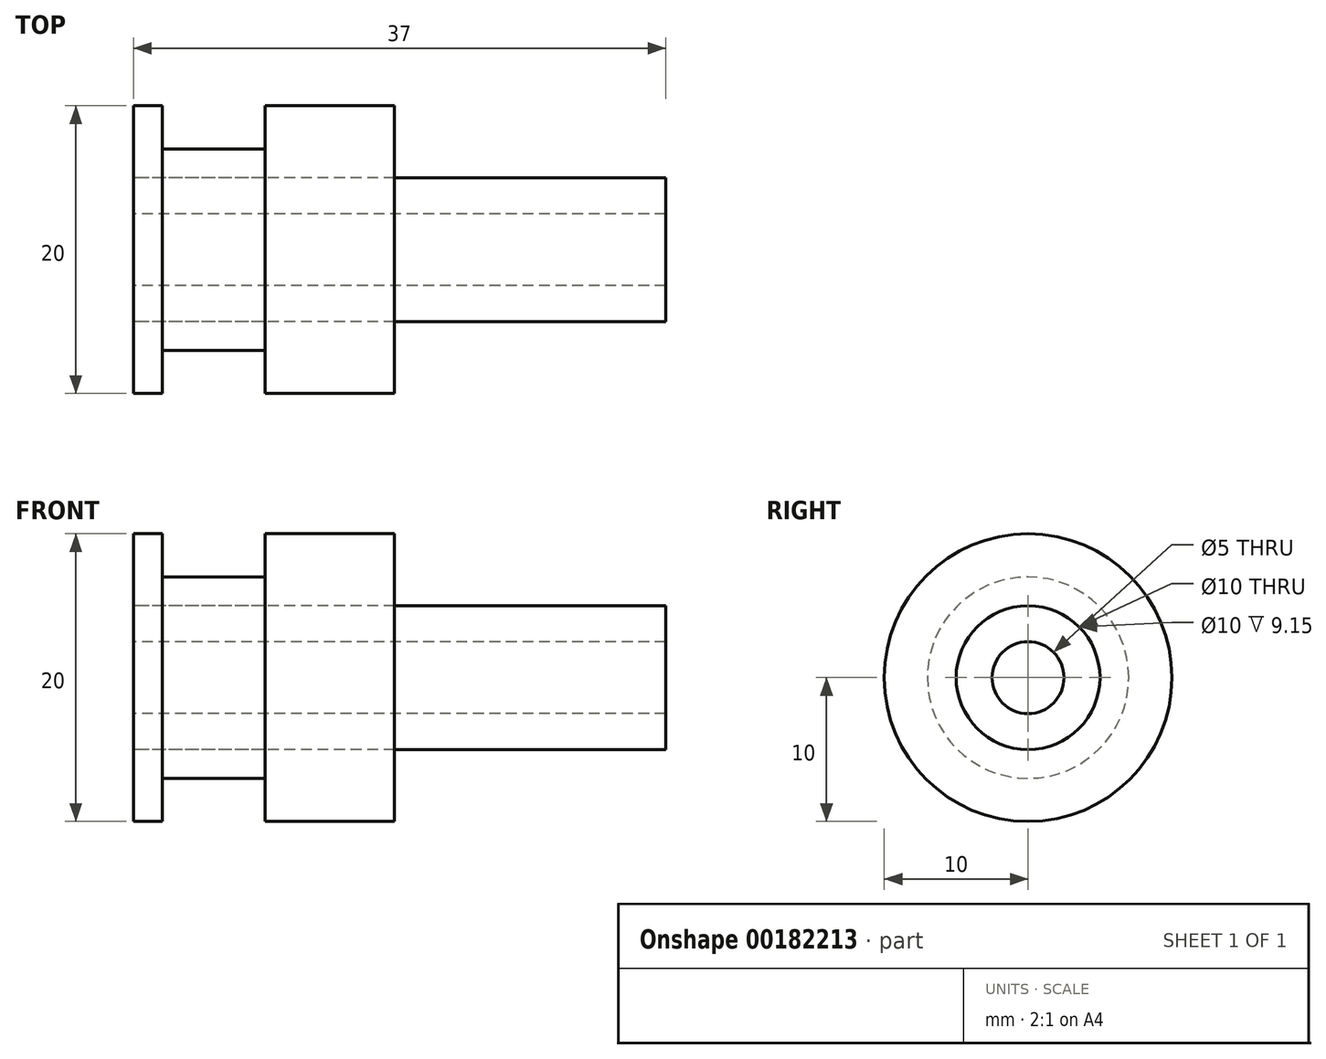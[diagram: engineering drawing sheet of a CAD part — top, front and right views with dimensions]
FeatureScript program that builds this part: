
annotation { "Feature Type Name" : "Feature", "Feature Type Description" : "" }
export const myFeature = defineFeature(function(context is Context, id is Id, definition is map)
    precondition{}
    {
        {
            assignVariable(context, id + "F0", {"name" : "Lt", "anyValue" : 6.35 * mm});
        }
        {
            assignVariable(context, id + "F1", {"name" : "LtSpcrClearance", "anyValue" : .8 * mm});
        }
        {
            assignVariable(context, id + "F2", {"name" : "ThrustWashThickness", "anyValue" : 2 * mm});
        }
        {
            var Q0;
            Q0=qCreatedBy(makeId("Right.planeOp"),FACE);
            var sketch = newSketch(context, id + "F3", { "sketchPlane" : qUnion([Q0])});
            skCircle(sketch, "E0", {"center": v(0, 0) * mm, "radius": 7 * mm});
            skCircle(sketch, "E1", {"center": v(0, 0) * mm, "radius": 5 * mm});
            skPoint(sketch, "E2", {"position": v(0, 5) * mm});
            skSolve(sketch);
        }
        {
            var Q0;
            Q0 = qSketchRegion(id + "F3", true);
            extrude(context, id + "F4", {"entities" : qUnion([Q0]), "depth" : getVariable(context, 'LtSpcrClearance') + getVariable(context, 'Lt')});
        }
        {
            var Q0;
            Q0=makeQuery(id+"F4.opExtrude","CAP_FACE",FACE,{"disambiguationData":[OSD([sQuery(id+"F3.wireOp",EDGE,"E0"),sQuery(id+"F3.wireOp",EDGE,"E1")])],"isStart":true});
            var sketch = newSketch(context, id + "F5", { "sketchPlane" : qUnion([Q0])});
            skCircle(sketch, "E3", {"center": v(0, 0) * mm, "radius": 10 * mm});
            skCircle(sketch, "E4", {"center": v(0, 0) * mm, "radius": 5 * mm});
            skSolve(sketch);
        }
        {
            var Q0;
            Q0 = qSketchRegion(id + "F5", true);
            extrude(context, id + "F6", {"entities" : qUnion([Q0]), "operationType" : NewBodyOperationType.ADD, "depth" : getVariable(context, 'ThrustWashThickness')});
        }
        {
            var Q0;
            Q0=makeQuery(id+"F4.opExtrude","CAP_FACE",FACE,{"disambiguationData":[OSD([sQuery(id+"F3.wireOp",EDGE,"E0"),sQuery(id+"F3.wireOp",EDGE,"E1")])],"isStart":false});
            var sketch = newSketch(context, id + "F7", { "sketchPlane" : qUnion([Q0])});
            skCircle(sketch, "E5", {"center": v(0, 0) * mm, "radius": 10 * mm});
            skCircle(sketch, "E6", {"center": v(0, 0) * mm, "radius": 5 * mm});
            skSolve(sketch);
        }
        {
            var Q0;
            Q0 = qSketchRegion(id + "F7", true);
            extrude(context, id + "F8", {"entities" : qUnion([Q0]), "depth" : 9 * mm});
        }
        {
            var Q0;
            Q0=makeQuery(id+"F6.opExtrude","CAP_FACE",FACE,{"disambiguationData":[OSD([sQuery(id+"F5.wireOp",EDGE,"E3"),sQuery(id+"F5.wireOp",EDGE,"E4")])],"isStart":false});
            var sketch = newSketch(context, id + "F9", { "sketchPlane" : qUnion([Q0])});
            skCircle(sketch, "E7", {"center": v(0, 0) * mm, "radius": 5 * mm});
            skSolve(sketch);
        }
        {
            var Q0;
            Q0 = qSketchRegion(id + "F9", true);
            extrude(context, id + "F10", {"entities" : qUnion([Q0]), "oppositeDirection" : true, "depth" : 37 * mm});
        }
        {
            var Q0;
            Q0=sQuery(id+"F9.wireOp",VERTEX,"E7.center");
            var Q1;
            Q1=makeQuery(id+"F10.opExtrude","SWEPT_BODY",BODY,{"disambiguationData":[OSD([sQuery(id+"F9.wireOp",EDGE,"E7")])]});
            hole(context, id + "F11", {"style" : HoleStyle.SIMPLE, "endStyle" : HoleEndStyle.THROUGH, "standardTappedOrClearance" : lookupTablePath({ "standard" : "ISO", "engagement" : "75%", "pitch" : "1 mm", "size" : "M6", "type" : "Tapped" }), "standardBlindInLast" : lookupTablePath({ "standard" : "ISO", "engagement" : "75%", "pitch" : "1 mm", "size" : "M6", "type" : "Tapped" }), "holeDiameter" : 5 * mm, "locations" : qUnion([Q0]), "scope" : qUnion([Q1]), "isTappedThrough" : true, "majorDiameter" : 6 * mm, "showTappedDepth" : true});
        }
    });
